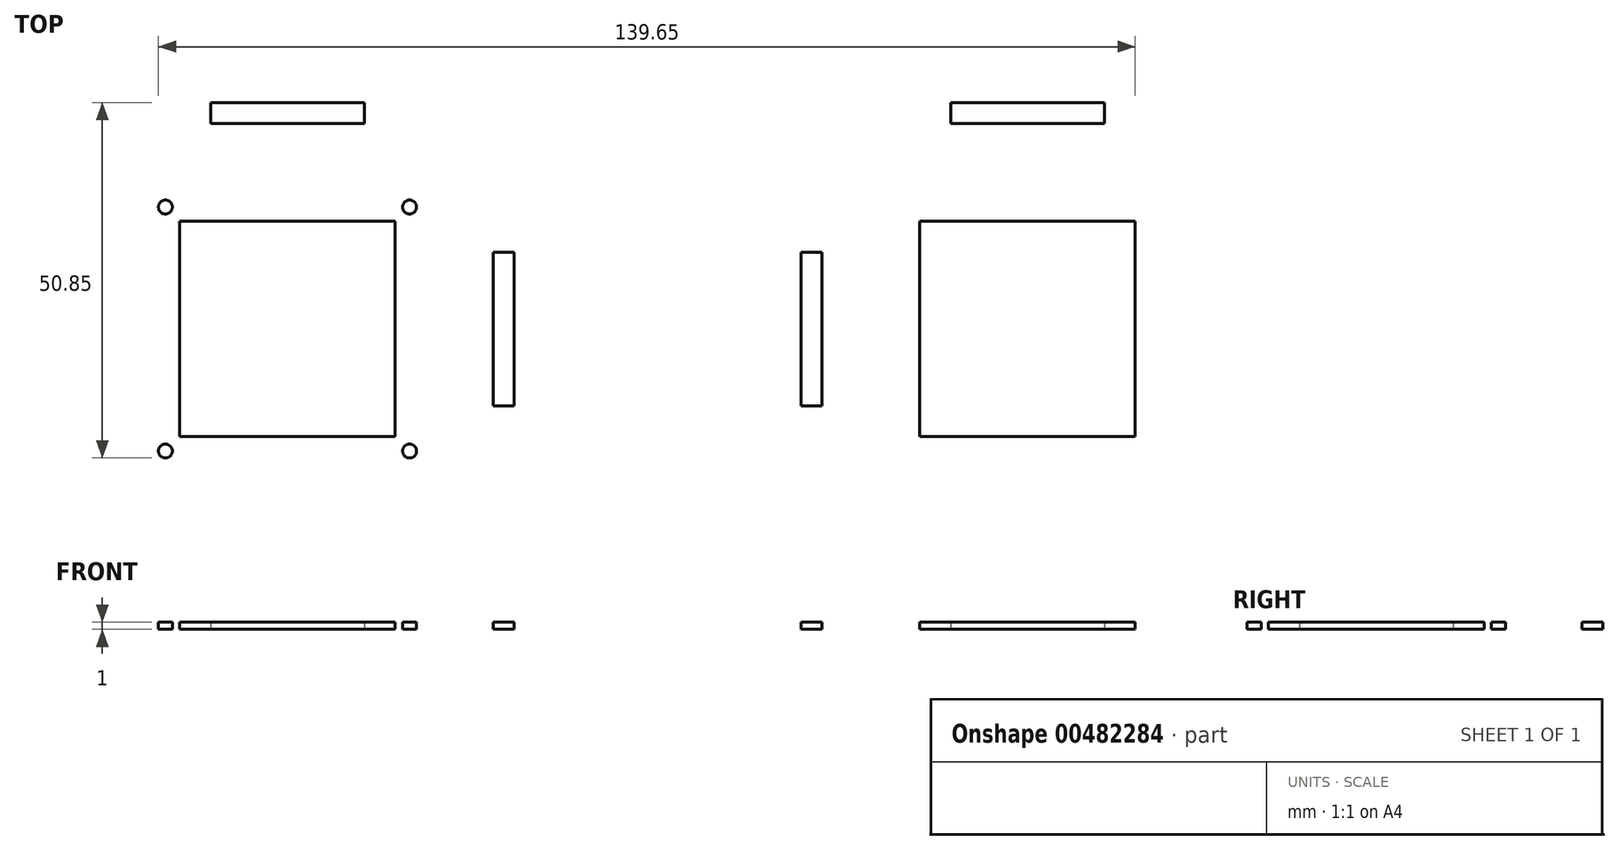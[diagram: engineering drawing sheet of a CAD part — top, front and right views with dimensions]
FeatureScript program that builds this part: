
annotation { "Feature Type Name" : "Feature", "Feature Type Description" : "" }
export const myFeature = defineFeature(function(context is Context, id is Id, definition is map)
    precondition{}
    {
        {
            var Q0;
            Q0=qCreatedBy(makeId("Top.planeOp"),FACE);
            var sketch = newSketch(context, id + "F0", { "sketchPlane" : qUnion([Q0])});
            skLineSegment(sketch, "E0.bottom", {"start": v(-68.3, 15.4) * mm, "end": v(-37.5, 15.4) * mm});
            skLineSegment(sketch, "E0.top", {"start": v(-68.3, -15.4) * mm, "end": v(-37.5, -15.4) * mm});
            skLineSegment(sketch, "E0.left", {"start": v(-68.3, 15.4) * mm, "end": v(-68.3, -15.4) * mm});
            skLineSegment(sketch, "E0.right", {"start": v(-37.5, 15.4) * mm, "end": v(-37.5, -15.4) * mm});
            skCircle(sketch, "E1", {"center": v(-70.35, 17.45) * mm, "radius": 1 * mm});
            skCircle(sketch, "E2", {"center": v(-35.45, 17.45) * mm, "radius": 1 * mm});
            skCircle(sketch, "E3", {"center": v(-35.45, -17.45) * mm, "radius": 1 * mm});
            skCircle(sketch, "E4", {"center": v(-70.35, -17.45) * mm, "radius": 1 * mm});
            skLineSegment(sketch, "E5", {"start": v(-52.9, 15.4) * mm, "end": v(-52.9, -15.4) * mm, "construction": true});
            skLineSegment(sketch, "E6", {"start": v(-68.3, 0) * mm, "end": v(-37.5, 0) * mm, "construction": true});
            skLineSegment(sketch, "E7.bottom", {"start": v(-23.5, 11) * mm, "end": v(-20.5, 11) * mm});
            skLineSegment(sketch, "E7.top", {"start": v(-23.5, -11) * mm, "end": v(-20.5, -11) * mm});
            skLineSegment(sketch, "E7.left", {"start": v(-23.5, 11) * mm, "end": v(-23.5, -11) * mm});
            skLineSegment(sketch, "E7.right", {"start": v(-20.5, 11) * mm, "end": v(-20.5, -11) * mm});
            skLineSegment(sketch, "E8.bottom", {"start": v(-63.9, 32.4) * mm, "end": v(-41.9, 32.4) * mm});
            skLineSegment(sketch, "E8.top", {"start": v(-63.9, 29.4) * mm, "end": v(-41.9, 29.4) * mm});
            skLineSegment(sketch, "E8.left", {"start": v(-63.9, 32.4) * mm, "end": v(-63.9, 29.4) * mm});
            skLineSegment(sketch, "E8.right", {"start": v(-41.9, 32.4) * mm, "end": v(-41.9, 29.4) * mm});
            skLineSegment(sketch, "E9.MirrorCS", {"start": v(63.9, 32.4) * mm, "end": v(63.9, 29.4) * mm});
            skLineSegment(sketch, "E10.MirrorCS", {"start": v(23.5, -11) * mm, "end": v(20.5, -11) * mm});
            skLineSegment(sketch, "E11.MirrorCS", {"start": v(23.5, 11) * mm, "end": v(20.5, 11) * mm});
            skLineSegment(sketch, "E12.MirrorCS", {"start": v(41.9, 32.4) * mm, "end": v(41.9, 29.4) * mm});
            skCircle(sketch, "E13.MirrorC", {"center": v(35.45, -17.45) * mm, "radius": 1 * mm});
            skCircle(sketch, "E14.MirrorC", {"center": v(35.45, 17.45) * mm, "radius": 1 * mm});
            skCircle(sketch, "E15.MirrorC", {"center": v(70.35, 17.45) * mm, "radius": 1 * mm});
            skCircle(sketch, "E16.MirrorC", {"center": v(70.35, -17.45) * mm, "radius": 1 * mm});
            skLineSegment(sketch, "E17.MirrorCS", {"start": v(23.5, 11) * mm, "end": v(23.5, -11) * mm});
            skLineSegment(sketch, "E18.MirrorCS", {"start": v(52.9, 15.4) * mm, "end": v(52.9, -15.4) * mm, "construction": true});
            skLineSegment(sketch, "E19.MirrorCS", {"start": v(68.3, 0) * mm, "end": v(37.5, 0) * mm, "construction": true});
            skLineSegment(sketch, "E20.MirrorCS", {"start": v(37.5, 15.4) * mm, "end": v(37.5, -15.4) * mm});
            skLineSegment(sketch, "E21.MirrorCS", {"start": v(68.3, 15.4) * mm, "end": v(68.3, -15.4) * mm});
            skLineSegment(sketch, "E22.MirrorCS", {"start": v(68.3, -15.4) * mm, "end": v(37.5, -15.4) * mm});
            skLineSegment(sketch, "E23.MirrorCS", {"start": v(68.3, 15.4) * mm, "end": v(37.5, 15.4) * mm});
            skLineSegment(sketch, "E24.MirrorCS", {"start": v(63.9, 29.4) * mm, "end": v(41.9, 29.4) * mm});
            skLineSegment(sketch, "E25.MirrorCS", {"start": v(63.9, 32.4) * mm, "end": v(41.9, 32.4) * mm});
            skLineSegment(sketch, "E26.MirrorCS", {"start": v(20.5, 11) * mm, "end": v(20.5, -11) * mm});
            skSolve(sketch);
        }
        {
            var Q0;
            Q0=makeQuery(id+"F0.imprint","IMPRINT",FACE,{"disambiguationData":[TD([[makeQuery(id+"F0.imprint","IMPRINT",EDGE,{"derivedFrom":sQuery(id+"F0.wireOp",EDGE,"E10.MirrorCS")}),-1.0]])]});
            var Q1;
            Q1=makeQuery(id+"F0.imprint","IMPRINT",FACE,{"disambiguationData":[TD([[makeQuery(id+"F0.imprint","IMPRINT",EDGE,{"derivedFrom":sQuery(id+"F0.wireOp",EDGE,"E9.MirrorCS")}),-1.0]])]});
            var Q2;
            Q2=makeQuery(id+"F0.imprint","IMPRINT",FACE,{"disambiguationData":[TD([[makeQuery(id+"F0.imprint","IMPRINT",EDGE,{"derivedFrom":sQuery(id+"F0.wireOp",EDGE,"E8.bottom")}),-1.0]])]});
            var Q3;
            Q3=makeQuery(id+"F0.imprint","IMPRINT",FACE,{"disambiguationData":[TD([[makeQuery(id+"F0.imprint","IMPRINT",EDGE,{"derivedFrom":sQuery(id+"F0.wireOp",EDGE,"E7.bottom")}),-1.0]])]});
            var Q4;
            Q4=makeQuery(id+"F0.imprint","IMPRINT",FACE,{"disambiguationData":[TD([[makeQuery(id+"F0.imprint","IMPRINT",EDGE,{"derivedFrom":sQuery(id+"F0.wireOp",EDGE,"E0.bottom")}),-1.0]])]});
            var Q5;
            Q5=makeQuery(id+"F0.imprint","IMPRINT",FACE,{"disambiguationData":[TD([[makeQuery(id+"F0.imprint","IMPRINT",EDGE,{"derivedFrom":sQuery(id+"F0.wireOp",EDGE,"E20.MirrorCS")}),1.0]])]});
            var Q6;
            Q6=makeQuery(id+"F0.imprint","IMPRINT",FACE,{"disambiguationData":[TD([[makeQuery(id+"F0.imprint","IMPRINT",EDGE,{"derivedFrom":sQuery(id+"F0.wireOp",EDGE,"E13.MirrorC")}),-1.0]])]});
            var Q7;
            Q7=makeQuery(id+"F0.imprint","IMPRINT",FACE,{"disambiguationData":[TD([[makeQuery(id+"F0.imprint","IMPRINT",EDGE,{"derivedFrom":sQuery(id+"F0.wireOp",EDGE,"E14.MirrorC")}),-1.0]])]});
            var Q8;
            Q8=makeQuery(id+"F0.imprint","IMPRINT",FACE,{"disambiguationData":[TD([[makeQuery(id+"F0.imprint","IMPRINT",EDGE,{"derivedFrom":sQuery(id+"F0.wireOp",EDGE,"E4")}),1.0]])]});
            var Q9;
            Q9=makeQuery(id+"F0.imprint","IMPRINT",FACE,{"disambiguationData":[TD([[makeQuery(id+"F0.imprint","IMPRINT",EDGE,{"derivedFrom":sQuery(id+"F0.wireOp",EDGE,"E1")}),1.0]])]});
            var Q10;
            Q10=makeQuery(id+"F0.imprint","IMPRINT",FACE,{"disambiguationData":[TD([[makeQuery(id+"F0.imprint","IMPRINT",EDGE,{"derivedFrom":sQuery(id+"F0.wireOp",EDGE,"E15.MirrorC")}),-1.0]])]});
            var Q11;
            Q11=makeQuery(id+"F0.imprint","IMPRINT",FACE,{"disambiguationData":[TD([[makeQuery(id+"F0.imprint","IMPRINT",EDGE,{"derivedFrom":sQuery(id+"F0.wireOp",EDGE,"E16.MirrorC")}),-1.0]])]});
            var Q12;
            Q12=makeQuery(id+"F0.imprint","IMPRINT",FACE,{"disambiguationData":[TD([[makeQuery(id+"F0.imprint","IMPRINT",EDGE,{"derivedFrom":sQuery(id+"F0.wireOp",EDGE,"E3")}),1.0]])]});
            var Q13;
            Q13=makeQuery(id+"F0.imprint","IMPRINT",FACE,{"disambiguationData":[TD([[makeQuery(id+"F0.imprint","IMPRINT",EDGE,{"derivedFrom":sQuery(id+"F0.wireOp",EDGE,"E2")}),1.0]])]});
            extrude(context, id + "F1", {"entities" : qUnion([Q0, Q1, Q2, Q3, Q4, Q5, Q6, Q7, Q8, Q9, Q10, Q11, Q12, Q13]), "depth" : 1 * mm});
        }
    });
